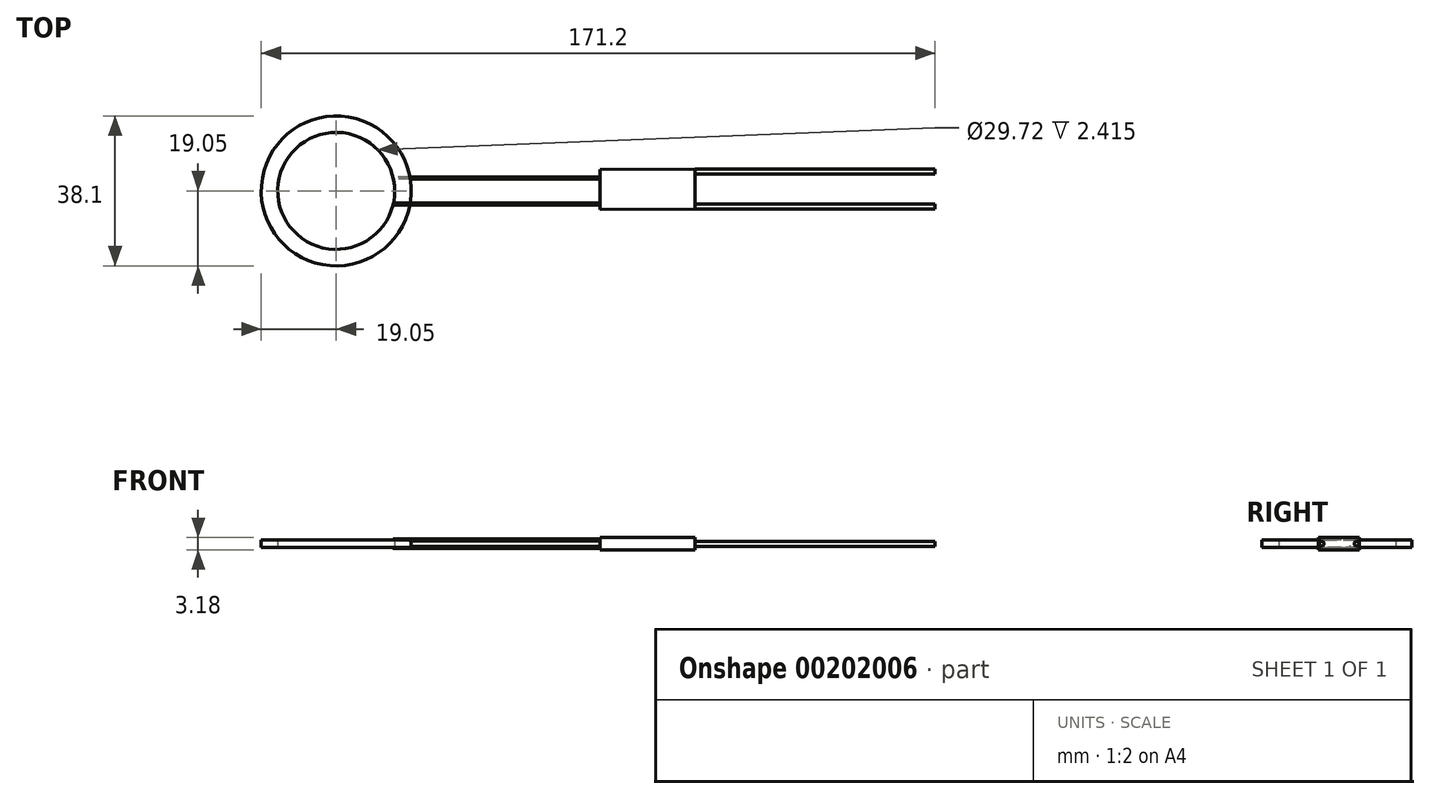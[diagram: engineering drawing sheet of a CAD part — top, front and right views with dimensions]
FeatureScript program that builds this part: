
annotation { "Feature Type Name" : "Feature", "Feature Type Description" : "" }
export const myFeature = defineFeature(function(context is Context, id is Id, definition is map)
    precondition{}
    {
        {
            var Q0;
            Q0=qCreatedBy(makeId("Top.planeOp"),FACE);
            var sketch = newSketch(context, id + "F0", { "sketchPlane" : qUnion([Q0])});
            skCircle(sketch, "E0", {"center": v(0, 0) * mm, "radius": 19.05 * mm});
            skCircle(sketch, "E1", {"center": v(0, 0) * mm, "radius": 14.86 * mm});
            skSolve(sketch);
        }
        {
            var Q0;
            Q0=makeQuery(id+"F0.imprint","IMPRINT",FACE,{"disambiguationData":[TD([[makeQuery(id+"F0.imprint","IMPRINT",EDGE,{"derivedFrom":sQuery(id+"F0.wireOp",EDGE,"E0")}),1.0]])]});
            extrude(context, id + "F1", {"entities" : qUnion([Q0]), "depth" : 1.9 * mm});
        }
        {
            var Q0;
            Q0=qCreatedBy(makeId("Right.planeOp"),FACE);
            var sketch = newSketch(context, id + "F2", { "sketchPlane" : qUnion([Q0])});
            skLineSegment(sketch, "E2", {"start": v(-3.3, 0) * mm, "end": v(3.3, 0) * mm, "construction": true});
            skLineSegment(sketch, "E3", {"start": v(0, 0) * mm, "end": v(0, 1.9) * mm, "construction": true});
            skCircle(sketch, "E4", {"center": v(3.3, 0) * mm, "radius": 0.25 * mm});
            skLineSegment(sketch, "E5", {"start": v(-3.3, 0) * mm, "end": v(-3.3, 1.9) * mm, "construction": true});
            skCircle(sketch, "E6", {"center": v(-3.3, 1.9) * mm, "radius": 0.25 * mm});
            skSolve(sketch);
        }
        {
            var Q0;
            Q0=makeQuery(id+"F2.imprint","IMPRINT",FACE,{"disambiguationData":[TD([[makeQuery(id+"F2.imprint","IMPRINT",EDGE,{"derivedFrom":sQuery(id+"F2.wireOp",EDGE,"E6")}),1.0]])]});
            var Q1;
            Q1=makeQuery(id+"F1.opExtrude","SWEPT_FACE",FACE,{"disambiguationData":[OSD([sQuery(id+"F0.wireOp",EDGE,"E0")])]});
            extrude(context, id + "F3", {"entities" : qUnion([Q0]), "operationType" : NewBodyOperationType.ADD, "depth" : 67.06 * mm});
        }
        {
            var Q0;
            Q0=makeQuery(id+"F2.imprint","IMPRINT",FACE,{"disambiguationData":[TD([[makeQuery(id+"F2.imprint","IMPRINT",EDGE,{"derivedFrom":sQuery(id+"F2.wireOp",EDGE,"E4")}),1.0]])]});
            extrude(context, id + "F4", {"entities" : qUnion([Q0]), "operationType" : NewBodyOperationType.ADD, "depth" : 67.06 * mm});
        }
        {
            var Q0;
            Q0=makeQuery(id+"F0.imprint","IMPRINT",FACE,{"disambiguationData":[TD([[makeQuery(id+"F0.imprint","IMPRINT",EDGE,{"derivedFrom":sQuery(id+"F0.wireOp",EDGE,"E1")}),1.0]])]});
            extrude(context, id + "F5", {"entities" : qUnion([Q0]), "operationType" : NewBodyOperationType.REMOVE, "endBound" : BoundingType.THROUGH_ALL, "oppositeDirection" : true, "depth" : 25.4 * mm, "hasSecondDirection" : true, "secondDirectionBound" : SecondDirectionBoundingType.THROUGH_ALL, "secondDirectionOppositeDirection" : false, "secondDirectionDepth" : 25.4 * mm});
        }
        {
            var Q0;
            Q0=qCreatedBy(makeId("Top.planeOp"),FACE);
            var sketch = newSketch(context, id + "F6", { "sketchPlane" : qUnion([Q0])});
            skLineSegment(sketch, "E7.bottom", {"start": v(67.06, 5.45) * mm, "end": v(91.19, 5.59) * mm});
            skLineSegment(sketch, "E7.left", {"start": v(67.06, 5.45) * mm, "end": v(67.06, -4.7) * mm});
            skLineSegment(sketch, "E7.right", {"start": v(91.19, 5.59) * mm, "end": v(91.19, -4.57) * mm});
            skLineSegment(sketch, "E8", {"start": v(67.06, -4.7) * mm, "end": v(91.19, -4.57) * mm});
            skLineSegment(sketch, "E9", {"start": v(67.06, 0.37) * mm, "end": v(0, 0) * mm, "construction": true});
            skSolve(sketch);
        }
        {
            var Q0;
            Q0=makeQuery(id+"F6.imprint","IMPRINT",FACE,{"disambiguationData":[TD([[makeQuery(id+"F6.imprint","IMPRINT",EDGE,{"derivedFrom":sQuery(id+"F6.wireOp",EDGE,"E7.bottom")}),-1.0]])]});
            extrude(context, id + "F7", {"entities" : qUnion([Q0]), "depth" : 2.54 * mm, "hasSecondDirection" : true, "secondDirectionOppositeDirection" : true, "secondDirectionDepth" : 0.64 * mm});
        }
        {
            var Q0;
            Q0=makeQuery(id+"F7.opExtrude","SWEPT_FACE",FACE,{"disambiguationData":[OSD([sQuery(id+"F6.wireOp",EDGE,"E7.right")])]});
            var sketch = newSketch(context, id + "F8", { "sketchPlane" : qUnion([Q0])});
            skLineSegment(sketch, "E10", {"start": v(-4.57, 0.95) * mm, "end": v(5.59, 0.95) * mm, "construction": true});
            skCircle(sketch, "E11", {"center": v(-3.94, 0.95) * mm, "radius": 0.64 * mm});
            skSolve(sketch);
        }
        {
            var Q0;
            Q0=makeQuery(id+"F8.imprint","IMPRINT",FACE,{"disambiguationData":[TD([[makeQuery(id+"F8.imprint","IMPRINT",EDGE,{"derivedFrom":sQuery(id+"F8.wireOp",EDGE,"E11")}),1.0]])]});
            extrude(context, id + "F9", {"entities" : qUnion([Q0]), "depth" : 60.96 * mm});
        }
        {
            var Q0;
            {var subQ3=sQuery(id+"F8.wireOp",EDGE,"E11");Q0=makeQuery(id+"F8.imprint","IMPRINT",FACE,{"disambiguationData":[TD([[makeQuery(id+"F8.imprint","IMPRINT",EDGE,{"derivedFrom":subQ3}),-1.0]])]});}
            var sketch = newSketch(context, id + "F10", { "sketchPlane" : qUnion([Q0])});
            skCircle(sketch, "E12", {"center": v(4.95, 0.95) * mm, "radius": 0.64 * mm});
            skSolve(sketch);
        }
        {
            var Q0;
            Q0=makeQuery(id+"F10.imprint","IMPRINT",FACE,{"disambiguationData":[TD([[makeQuery(id+"F10.imprint","IMPRINT",EDGE,{"derivedFrom":sQuery(id+"F10.wireOp",EDGE,"E12")}),1.0]])]});
            extrude(context, id + "F11", {"entities" : qUnion([Q0]), "depth" : 60.96 * mm});
        }
    });
